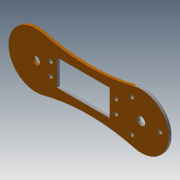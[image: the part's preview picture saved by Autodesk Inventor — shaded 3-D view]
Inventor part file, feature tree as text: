
AUTODESK INVENTOR PART (.ipt)
format: ipt  version: 2013 (Build 170138000, 138)  size: 308,224 bytes
history: native  units: mm
features: extrude x21, sketch x21
ambient origin geometry x8: Origin, YZ Plane, XZ Plane, XY Plane, X Axis, Y Axis, Z Axis, Center Point
bodies: Solid1 (feature_tree)
feature tree (42):
  extrude  "Extrusion1"  Depth=2.0mm TaperAngle=0.0deg
  extrude  "Extrusion2"  Depth=3.0mm
  extrude  "Extrusion3"  Depth=2.0mm TaperAngle=0.0deg
  extrude  "Extrusion4"  Depth=6.0mm
  extrude  "Extrusion5"  Depth=3.0mm
  extrude  "Extrusion6"  Depth=3.0mm
  extrude  "Extrusion7"  Depth=29.5mm
  extrude  "Extrusion8"  Depth=40.2mm
  extrude  "Extrusion9"  Depth=3.0mm
  extrude  "Extrusion10"  Depth=40.2mm
  extrude  "Extrusion11"  Depth=2.0mm TaperAngle=0.0deg
  extrude  "Extrusion12"  Depth=49.7mm
  extrude  "Extrusion13"  Depth=3.0mm
  sketch  "Sketch14"  dims[d74=3.0mm d75=2.0mm d76=0.0mm]
  sketch  "Sketch15"  dims[d77=2.0mm d78=0.0mm d79=2.0mm d80=0.0mm]
  sketch  "Sketch16"  dims[d81=2.0mm d82=0.0mm d83=2.0mm d84=0.0mm]
  extrude  "Extrusion14"  Depth=2.0mm TaperAngle=0.0deg
  extrude  "Extrusion15"  Depth=2.0mm TaperAngle=0.0deg
  extrude  "Extrusion16"  Depth=2.0mm TaperAngle=0.0deg
  extrude  "Extrusion17"  Depth=2.0mm TaperAngle=0.0deg
  extrude  "Extrusion18"  Depth=2.0mm TaperAngle=0.0deg
  extrude  "Extrusion19"  Depth=6.0mm
  extrude  "Extrusion20"  Depth=34.65mm
  extrude  "Extrusion21"  Depth=20.0mm
  sketch  "Sketch1"  dims[d1=6.0mm d3=10.0mm d5=4.0mm d7=4.0mm d8=2.0mm d9=0.0mm]
  sketch  "Sketch2"  dims[d11=3.0mm d14=3.0mm]
  sketch  "Sketch3"  dims[d15=3.0mm d16=2.0mm d17=0.0mm]
  sketch  "Sketch4"  dims[d18=10.5mm d19=6.0mm]
  sketch  "Sketch5"  dims[d20=2.0mm d21=0.0mm d33=3.0mm]
  sketch  "Sketch6"  dims[d34=3.0mm d35=3.0mm]
  sketch  "Sketch7"  dims[d36=2.0mm d37=0.0mm d46=29.5mm]
  sketch  "Sketch8"  dims[d48=10.7mm d49=40.2mm]
  sketch  "Sketch9"  dims[d57=3.0mm d58=3.0mm]
  sketch  "Sketch10"  dims[d63=2.0mm d64=0.0mm d65=40.2mm]
  sketch  "Sketch11"  dims[d66=20.0mm d67=2.0mm d68=0.0mm]
  sketch  "Sketch12"  dims[d69=2.0mm d70=0.0mm d71=49.7mm]
  sketch  "Sketch13"  dims[d72=49.7mm d73=3.0mm]
  sketch  "Sketch17"  dims[d85=2.0mm d86=0.0mm d87=2.0mm d88=0.0mm]
  sketch  "Sketch18"  dims[d89=2.0mm d90=0.0mm d91=2.0mm d92=0.0mm]
  sketch  "Sketch19"  dims[d93=2.0mm d94=0.0mm d95=6.0mm]
  sketch  "Sketch20"  dims[d96=2.0mm d97=0.0mm d100=34.65mm]
  sketch  "Sketch21"  dims[d103=40.2mm d104=20.0mm d109=3.0mm d110=3.0mm d111=49.7mm d112=49.7mm d113=3.0mm d114=3.0mm d115=2.0mm d116=0.0mm d120=3.0mm d121=3.0mm d123=2.0mm d124=0.0mm d125=2.0mm d126=0.0mm]
